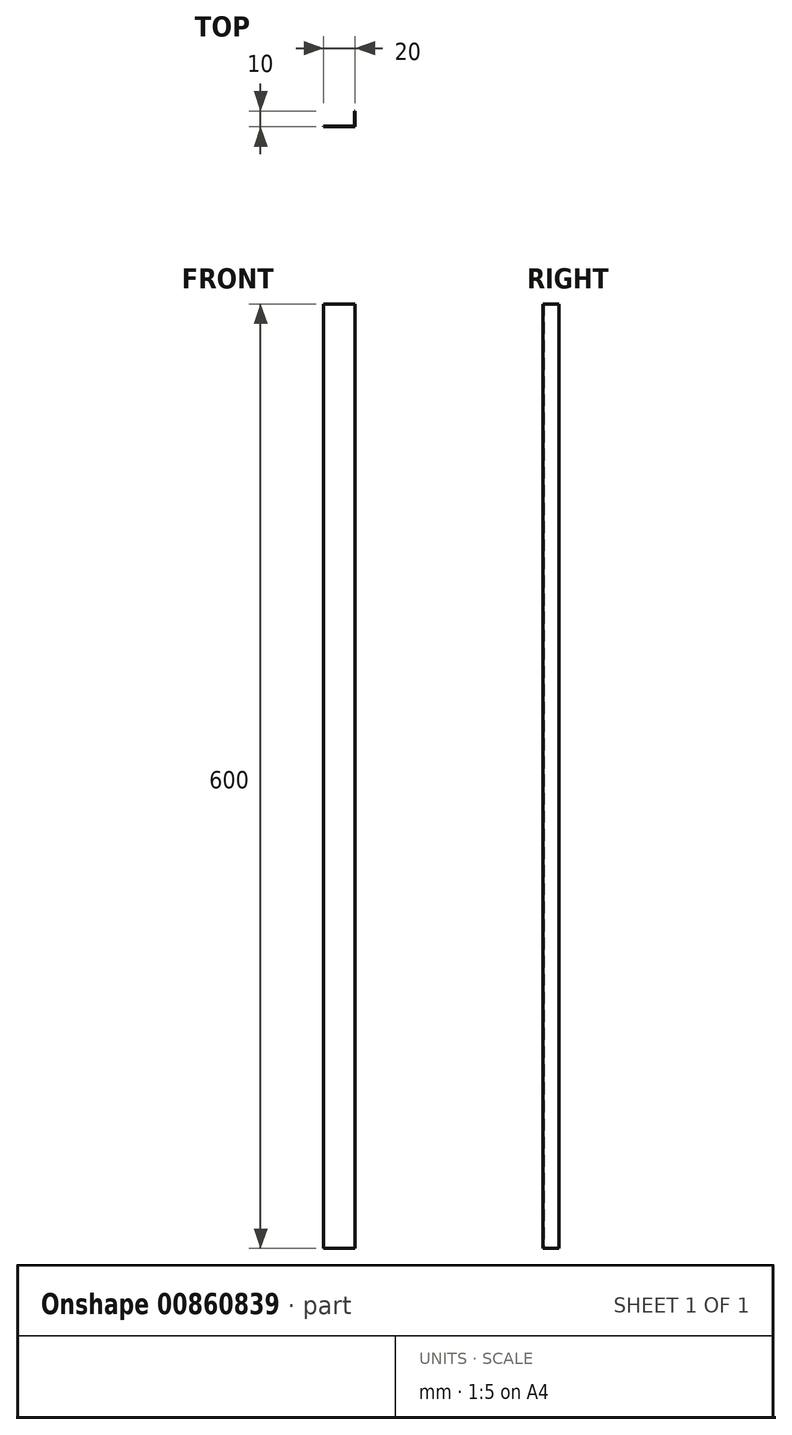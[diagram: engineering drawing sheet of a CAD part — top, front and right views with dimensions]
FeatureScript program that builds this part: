
annotation { "Feature Type Name" : "Feature", "Feature Type Description" : "" }
export const myFeature = defineFeature(function(context is Context, id is Id, definition is map)
    precondition{}
    {
        {
            var Q0;
            Q0=qCreatedBy(makeId("Top.planeOp"),FACE);
            var sketch = newSketch(context, id + "F0", { "sketchPlane" : qUnion([Q0])});
            skLineSegment(sketch, "E0.bottom", {"start": v(-27.92, -20.5) * mm, "end": v(-7.92, -20.5) * mm});
            skLineSegment(sketch, "E0.top", {"start": v(-27.92, -21) * mm, "end": v(-7.92, -21) * mm});
            skLineSegment(sketch, "E0.left", {"start": v(-27.92, -20.5) * mm, "end": v(-27.92, -21) * mm});
            skLineSegment(sketch, "E0.right", {"start": v(-7.92, -20.5) * mm, "end": v(-7.92, -21) * mm});
            skLineSegment(sketch, "E1.bottom", {"start": v(-7.92, -21) * mm, "end": v(-8.42, -21) * mm});
            skLineSegment(sketch, "E1.top", {"start": v(-7.92, -11) * mm, "end": v(-8.42, -11) * mm});
            skLineSegment(sketch, "E1.left", {"start": v(-7.92, -21) * mm, "end": v(-7.92, -11) * mm});
            skLineSegment(sketch, "E1.right", {"start": v(-8.42, -21) * mm, "end": v(-8.42, -11) * mm});
            skSolve(sketch);
        }
        {
            var Q0;
            {var subQ4=sQuery(id+"F0.wireOp",EDGE,"E0.top");Q0=makeQuery(id+"F0.imprint","IMPRINT",FACE,{"disambiguationData":[TD([[makeQuery(id+"F0.imprint","IMPRINT",EDGE,{"derivedFrom":subQ4}),1.0]])]});}
            var Q1;
            {var subQ5=sQuery(id+"F0.wireOp",EDGE,"E1.bottom");Q1=makeQuery(id+"F0.imprint","IMPRINT",FACE,{"disambiguationData":[TD([[makeQuery(id+"F0.imprint","IMPRINT",EDGE,{"derivedFrom":subQ5}),-1.0]])]});}
            var Q2;
            {var subQ5=sQuery(id+"F0.wireOp",EDGE,"E1.top");Q2=makeQuery(id+"F0.imprint","IMPRINT",FACE,{"disambiguationData":[TD([[makeQuery(id+"F0.imprint","IMPRINT",EDGE,{"derivedFrom":subQ5}),1.0]])]});}
            extrude(context, id + "F1", {"entities" : qUnion([Q0, Q1, Q2]), "depth" : 600 * mm, "offsetDistance" : 25 * mm});
        }
    });
